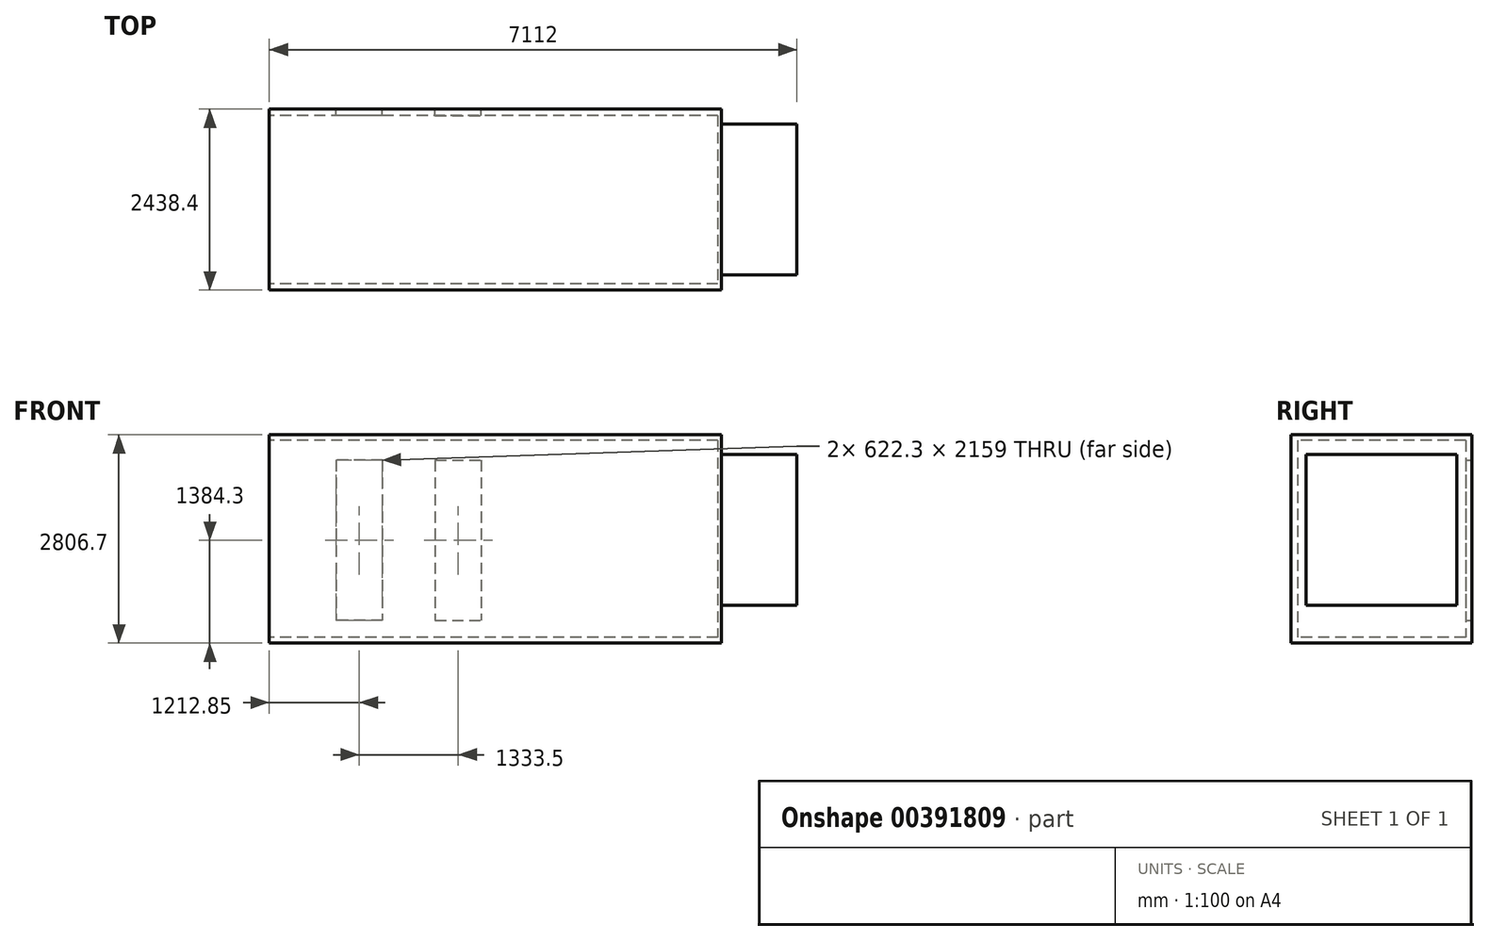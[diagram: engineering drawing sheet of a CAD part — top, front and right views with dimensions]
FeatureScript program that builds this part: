
annotation { "Feature Type Name" : "Feature", "Feature Type Description" : "" }
export const myFeature = defineFeature(function(context is Context, id is Id, definition is map)
    precondition{}
    {
        {
            var Q0;
            Q0=qCreatedBy(makeId("Top.planeOp"),FACE);
            var sketch = newSketch(context, id + "F0", { "sketchPlane" : qUnion([Q0])});
            skLineSegment(sketch, "E0.bottom", {"start": v(3048, -1219.2) * mm, "end": v(-3048, -1219.2) * mm});
            skLineSegment(sketch, "E0.top", {"start": v(3048, 1219.2) * mm, "end": v(-3048, 1219.2) * mm});
            skLineSegment(sketch, "E0.left", {"start": v(3048, -1219.2) * mm, "end": v(3048, 1219.2) * mm});
            skLineSegment(sketch, "E0.right", {"start": v(-3048, -1219.2) * mm, "end": v(-3048, 1219.2) * mm});
            skPoint(sketch, "E0.middle", {"position": v(0, 0) * mm});
            skSolve(sketch);
        }
        {
            var Q0;
            Q0 = qSketchRegion(id + "F0", true);
            extrude(context, id + "F1", {"entities" : qUnion([Q0]), "depth" : 2806.7 * mm});
        }
        {
            var Q0;
            Q0=makeQuery(id+"F1.opExtrude","SWEPT_FACE",FACE,{"disambiguationData":[OSD([sQuery(id+"F0.wireOp",EDGE,"E0.left")])]});
            var sketch = newSketch(context, id + "F2", { "sketchPlane" : qUnion([Q0])});
            skLineSegment(sketch, "E1.bottom", {"start": v(-1016, 2540) * mm, "end": v(1016, 2540) * mm});
            skLineSegment(sketch, "E1.top", {"start": v(-1016, 508) * mm, "end": v(1016, 508) * mm});
            skLineSegment(sketch, "E1.left", {"start": v(-1016, 2540) * mm, "end": v(-1016, 508) * mm});
            skLineSegment(sketch, "E1.right", {"start": v(1016, 2540) * mm, "end": v(1016, 508) * mm});
            skPoint(sketch, "E1.middle", {"position": v(0, 1524) * mm});
            skSolve(sketch);
        }
        {
            var Q0;
            Q0=makeQuery(id+"F1.opExtrude","SWEPT_FACE",FACE,{"disambiguationData":[OSD([sQuery(id+"F0.wireOp",EDGE,"E0.right")])]});
            var sketch = newSketch(context, id + "F3", { "sketchPlane" : qUnion([Q0])});
            skLineSegment(sketch, "E2.bottom", {"start": v(-1133.98, 2730.98) * mm, "end": v(1133.98, 2730.98) * mm});
            skLineSegment(sketch, "E2.top", {"start": v(-1133.98, 75.72) * mm, "end": v(1133.98, 75.72) * mm});
            skLineSegment(sketch, "E2.left", {"start": v(-1133.98, 2730.98) * mm, "end": v(-1133.98, 75.72) * mm});
            skLineSegment(sketch, "E2.right", {"start": v(1133.98, 2730.98) * mm, "end": v(1133.98, 75.72) * mm});
            skPoint(sketch, "E2.middle", {"position": v(0, 1403.35) * mm});
            skPoint(sketch, "E2.middle.positionSnap0", {"position": v(-1219.2, 1403.35) * mm});
            skPoint(sketch, "E2.centerSnap0", {"position": v(-1219.2, 1403.35) * mm});
            skSolve(sketch);
        }
        {
            var Q0;
            Q0 = qSketchRegion(id + "F3", true);
            extrude(context, id + "F4", {"entities" : qUnion([Q0]), "operationType" : NewBodyOperationType.REMOVE, "oppositeDirection" : true, "depth" : 6045.2 * mm});
        }
        {
            var Q0;
            Q0=makeQuery(id+"F1.opExtrude","SWEPT_FACE",FACE,{"disambiguationData":[OSD([sQuery(id+"F0.wireOp",EDGE,"E0.top")])]});
            var sketch = newSketch(context, id + "F5", { "sketchPlane" : qUnion([Q0])});
            skLineSegment(sketch, "E3.bottom", {"start": v(1524, 2463.8) * mm, "end": v(2146.3, 2463.8) * mm});
            skLineSegment(sketch, "E3.top", {"start": v(1524, 304.8) * mm, "end": v(2146.3, 304.8) * mm});
            skLineSegment(sketch, "E3.left", {"start": v(1524, 2463.8) * mm, "end": v(1524, 304.8) * mm});
            skLineSegment(sketch, "E3.right", {"start": v(2146.3, 2463.8) * mm, "end": v(2146.3, 304.8) * mm});
            skPoint(sketch, "E3.middle", {"position": v(1835.15, 1384.3) * mm});
            skLineSegment(sketch, "E4.bottom", {"start": v(812.8, 2463.8) * mm, "end": v(190.5, 2463.8) * mm});
            skLineSegment(sketch, "E4.top", {"start": v(812.8, 304.8) * mm, "end": v(190.5, 304.8) * mm});
            skLineSegment(sketch, "E4.left", {"start": v(812.8, 2463.8) * mm, "end": v(812.8, 304.8) * mm});
            skLineSegment(sketch, "E4.right", {"start": v(190.5, 2463.8) * mm, "end": v(190.5, 304.8) * mm});
            skPoint(sketch, "E4.middle", {"position": v(501.65, 1384.3) * mm});
            skPoint(sketch, "E4.middle.positionSnap0", {"position": v(2146.3, 1384.3) * mm});
            skPoint(sketch, "E4.centerSnap0", {"position": v(2146.3, 1384.3) * mm});
            skSolve(sketch);
        }
        {
            var Q0;
            Q0 = qSketchRegion(id + "F5", true);
            extrude(context, id + "F6", {"entities" : qUnion([Q0]), "operationType" : NewBodyOperationType.REMOVE, "oppositeDirection" : true, "depth" : 254 * mm});
        }
        {
            var Q0;
            Q0=makeQuery(id+"F2.imprint","IMPRINT",FACE,{"disambiguationData":[TD([[makeQuery(id+"F2.imprint","IMPRINT",EDGE,{"derivedFrom":sQuery(id+"F2.wireOp",EDGE,"E1.bottom")}),-1.0]])]});
            extrude(context, id + "F7", {"entities" : qUnion([Q0]), "operationType" : NewBodyOperationType.ADD, "depth" : 1016 * mm});
        }
    });
